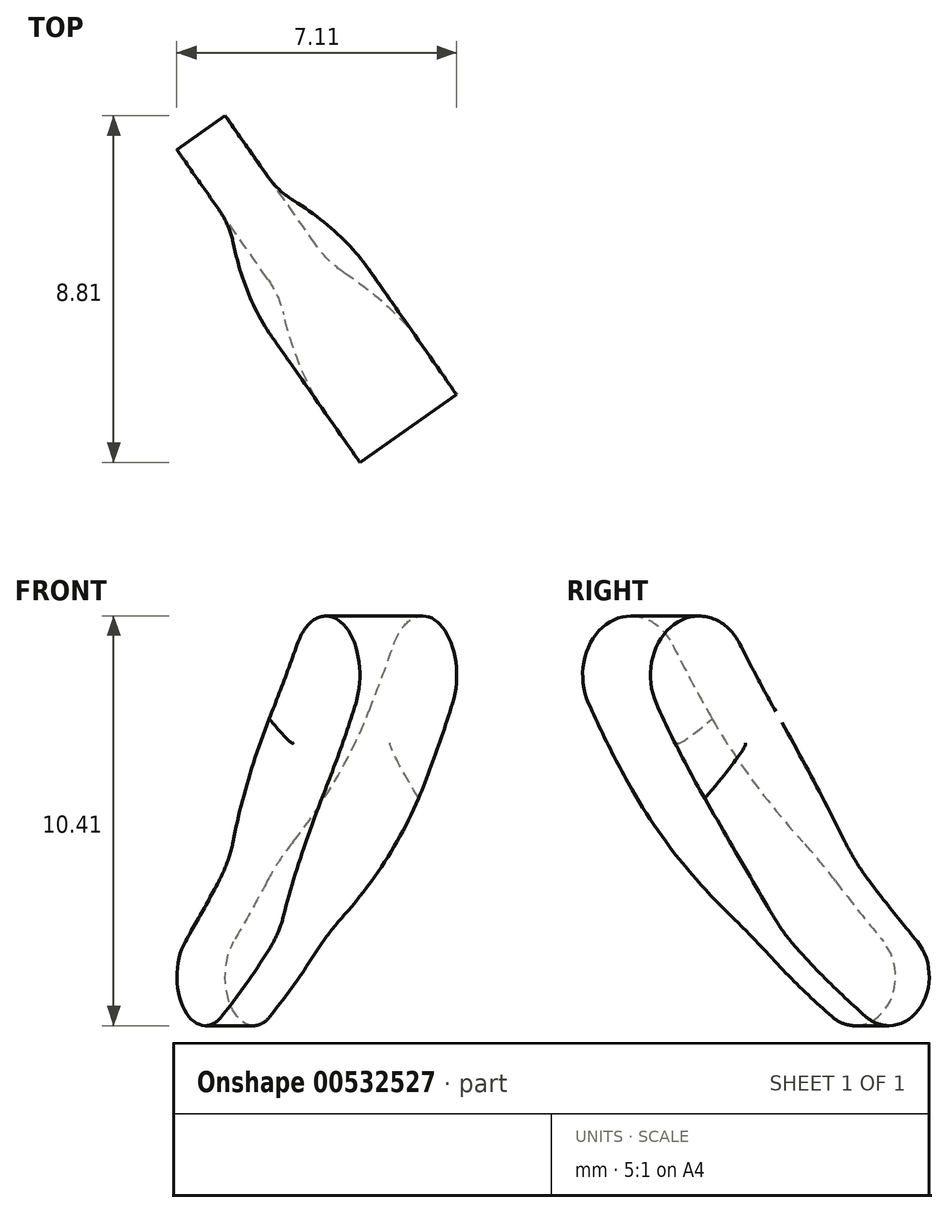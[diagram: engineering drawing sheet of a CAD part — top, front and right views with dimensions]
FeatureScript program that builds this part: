
annotation { "Feature Type Name" : "Feature", "Feature Type Description" : "" }
export const myFeature = defineFeature(function(context is Context, id is Id, definition is map)
    precondition{}
    {
        {
            var Q0;
            Q0=qCreatedBy(makeId("Top.planeOp"),FACE);
            var sketch = newSketch(context, id + "F0", { "sketchPlane" : qUnion([Q0])});
            skLineSegment(sketch, "E0", {"start": v(0, -2.05) * mm, "end": v(0, 2.29) * mm, "construction": true});
            skLineSegment(sketch, "E1", {"start": v(0, 2.29) * mm, "end": v(-4, 8) * mm});
            skLineSegment(sketch, "E2", {"start": v(0, -2.05) * mm, "end": v(-4.25, -4.5) * mm});
            skLineSegment(sketch, "E3", {"start": v(0, 0) * mm, "end": v(-4.5, 0.4) * mm});
            skSolve(sketch);
        }
        {
            var Q0;
            Q0=sQuery(id+"F0.wireOp",EDGE,"E1");
            cPlane(context, id + "F1", {"entities" : qUnion([Q0]), "cplaneType" : CPlaneType.LINE_ANGLE, "offset" : 25 * mm, "angle" : 90 * degree, "width" : 150 * mm, "height" : 150 * mm});
        }
        {
            var Q0;
            Q0=sQuery(id+"F0.wireOp",EDGE,"E3");
            cPlane(context, id + "F2", {"entities" : qUnion([Q0]), "cplaneType" : CPlaneType.LINE_ANGLE, "offset" : 25 * mm, "angle" : 0 * degree, "width" : 150 * mm, "height" : 150 * mm});
        }
        {
            var Q0;
            Q0=sQuery(id+"F0.wireOp",EDGE,"E2");
            cPlane(context, id + "F3", {"entities" : qUnion([Q0]), "cplaneType" : CPlaneType.LINE_ANGLE, "offset" : 25 * mm, "angle" : 0 * degree, "width" : 150 * mm, "height" : 150 * mm});
        }
        {
            var Q0;
            Q0=qCreatedBy(id+"F1.planeOp",FACE);
            var sketch = newSketch(context, id + "F4", { "sketchPlane" : qUnion([Q0])});
            skLineSegment(sketch, "E4.0", {"start": v(1.87, 0) * mm, "end": v(8.85, 0) * mm, "construction": true});
            skLineSegment(sketch, "E5", {"start": v(1.87, 0) * mm, "end": v(8.85, 2.54) * mm, "construction": true});
            skCircle(sketch, "E6", {"center": v(8.85, 2.54) * mm, "radius": 1.5 * mm});
            skLineSegment(sketch, "E7", {"start": v(8.85, 2.54) * mm, "end": v(15.28, -5.12) * mm, "construction": true});
            skLineSegment(sketch, "E8", {"start": v(15.28, -5.12) * mm, "end": v(6.28, -15.85) * mm, "construction": true});
            skLineSegment(sketch, "E9", {"start": v(6.28, -15.85) * mm, "end": v(1.58, -17.56) * mm, "construction": true});
            skLineSegment(sketch, "E10", {"start": v(1.58, -17.56) * mm, "end": v(1.98, -18.77) * mm, "construction": true});
            skCircle(sketch, "E11", {"center": v(15.28, -5.12) * mm, "radius": 1.25 * mm});
            skCircle(sketch, "E12", {"center": v(6.28, -15.85) * mm, "radius": 1 * mm});
            skSolve(sketch);
        }
        {
            var Q0;
            Q0=qCreatedBy(id+"F1.planeOp",FACE);
            var sketch = newSketch(context, id + "F5", { "sketchPlane" : qUnion([Q0])});
            skArc(sketch, "E13.0", {"start": v(14.55, -6.14) * mm, "mid": v(16.23, -5.93) * mm, "end": v(16.15, -4.23) * mm});
            skArc(sketch, "E13.1", {"start": v(10.13, 3.32) * mm, "mid": v(8.1, 3.84) * mm, "end": v(7.53, 1.82) * mm});
            skLineSegment(sketch, "E13.2", {"start": v(8.85, 2.54) * mm, "end": v(15.28, -5.12) * mm, "construction": true});
            skArc(sketch, "E14", {"start": v(10.13, 3.32) * mm, "mid": v(12.9, -0.64) * mm, "end": v(16.15, -4.23) * mm});
            skArc(sketch, "E15", {"start": v(7.53, 1.82) * mm, "mid": v(10.59, -2.55) * mm, "end": v(14.55, -6.14) * mm});
            skLineSegment(sketch, "E16", {"start": v(16.15, -4.23) * mm, "end": v(10.13, 3.32) * mm, "construction": true});
            skLineSegment(sketch, "E17", {"start": v(7.53, 1.82) * mm, "end": v(14.55, -6.14) * mm, "construction": true});
            skPoint(sketch, "E18", {"position": v(13.14, -0.45) * mm});
            skPoint(sketch, "E19", {"position": v(12.9, -0.64) * mm});
            skPoint(sketch, "E20", {"position": v(11.04, -2.16) * mm});
            skPoint(sketch, "E21", {"position": v(10.59, -2.55) * mm});
            skSolve(sketch);
        }
        {
            var Q0;
            Q0 = qSketchRegion(id + "F5", true);
            extrude(context, id + "F6", {"entities" : qUnion([Q0]), "endBound" : BoundingType.SYMMETRIC, "depth" : 3 * mm, "offsetDistance" : 25 * mm});
        }
        {
            var Q0;
            Q0=sQuery(id+"F4.wireOp",EDGE,"E7");
            cPlane(context, id + "F7", {"entities" : qUnion([Q0]), "cplaneType" : CPlaneType.LINE_ANGLE, "offset" : 25 * mm, "angle" : 47.5 * degree, "width" : 150 * mm, "height" : 150 * mm});
        }
        {
            var Q0;
            Q0=qCreatedBy(id+"F7.planeOp",FACE);
            var sketch = newSketch(context, id + "F8", { "sketchPlane" : qUnion([Q0])});
            skLineSegment(sketch, "E22.0", {"start": v(-0.33, 3.96) * mm, "end": v(-4.44, 13.07) * mm, "construction": true});
            skLineSegment(sketch, "E23", {"start": v(0.28, 2.59) * mm, "end": v(1.65, 3.2) * mm});
            skLineSegment(sketch, "E24", {"start": v(1.65, 3.2) * mm, "end": v(0.11, 6.62) * mm});
            skLineSegment(sketch, "E25", {"start": v(-4.95, 14.21) * mm, "end": v(-4.27, 14.52) * mm});
            skLineSegment(sketch, "E26", {"start": v(-4.27, 14.52) * mm, "end": v(-2.83, 11.33) * mm});
            skLineSegment(sketch, "E27", {"start": v(0.42, 5.94) * mm, "end": v(-0.95, 5.32) * mm, "construction": true});
            skLineSegment(sketch, "E28", {"start": v(-3.92, 11.93) * mm, "end": v(-3.24, 12.24) * mm, "construction": true});
            skArc(sketch, "E29", {"start": v(0.11, 6.62) * mm, "mid": v(-0.88, 8.48) * mm, "end": v(-2.11, 10.18) * mm});
            skArc(sketch, "E30", {"start": v(-2.11, 10.18) * mm, "mid": v(-2.51, 10.73) * mm, "end": v(-2.83, 11.33) * mm});
            skLineSegment(sketch, "E31.MirrorCS", {"start": v(-4.95, 14.21) * mm, "end": v(-5.63, 13.9) * mm});
            skLineSegment(sketch, "E32.MirrorCS", {"start": v(-5.63, 13.9) * mm, "end": v(-4.2, 10.71) * mm});
            skArc(sketch, "E33.MirrorCS", {"start": v(-2.62, 5.4) * mm, "mid": v(-3.36, 7.36) * mm, "end": v(-3.81, 9.42) * mm});
            skArc(sketch, "E34.MirrorCS", {"start": v(-3.81, 9.42) * mm, "mid": v(-3.96, 10.08) * mm, "end": v(-4.2, 10.71) * mm});
            skLineSegment(sketch, "E35.MirrorCS", {"start": v(0.28, 2.59) * mm, "end": v(-1.08, 1.97) * mm});
            skLineSegment(sketch, "E36.MirrorCS", {"start": v(-1.08, 1.97) * mm, "end": v(-2.62, 5.4) * mm});
            skSolve(sketch);
        }
        {
            var Q0;
            Q0 = qSketchRegion(id + "F8", true);
            extrude(context, id + "F9", {"entities" : qUnion([Q0]), "operationType" : NewBodyOperationType.INTERSECT, "endBound" : BoundingType.SYMMETRIC, "depth" : 5 * mm, "offsetDistance" : 25 * mm});
        }
    });
